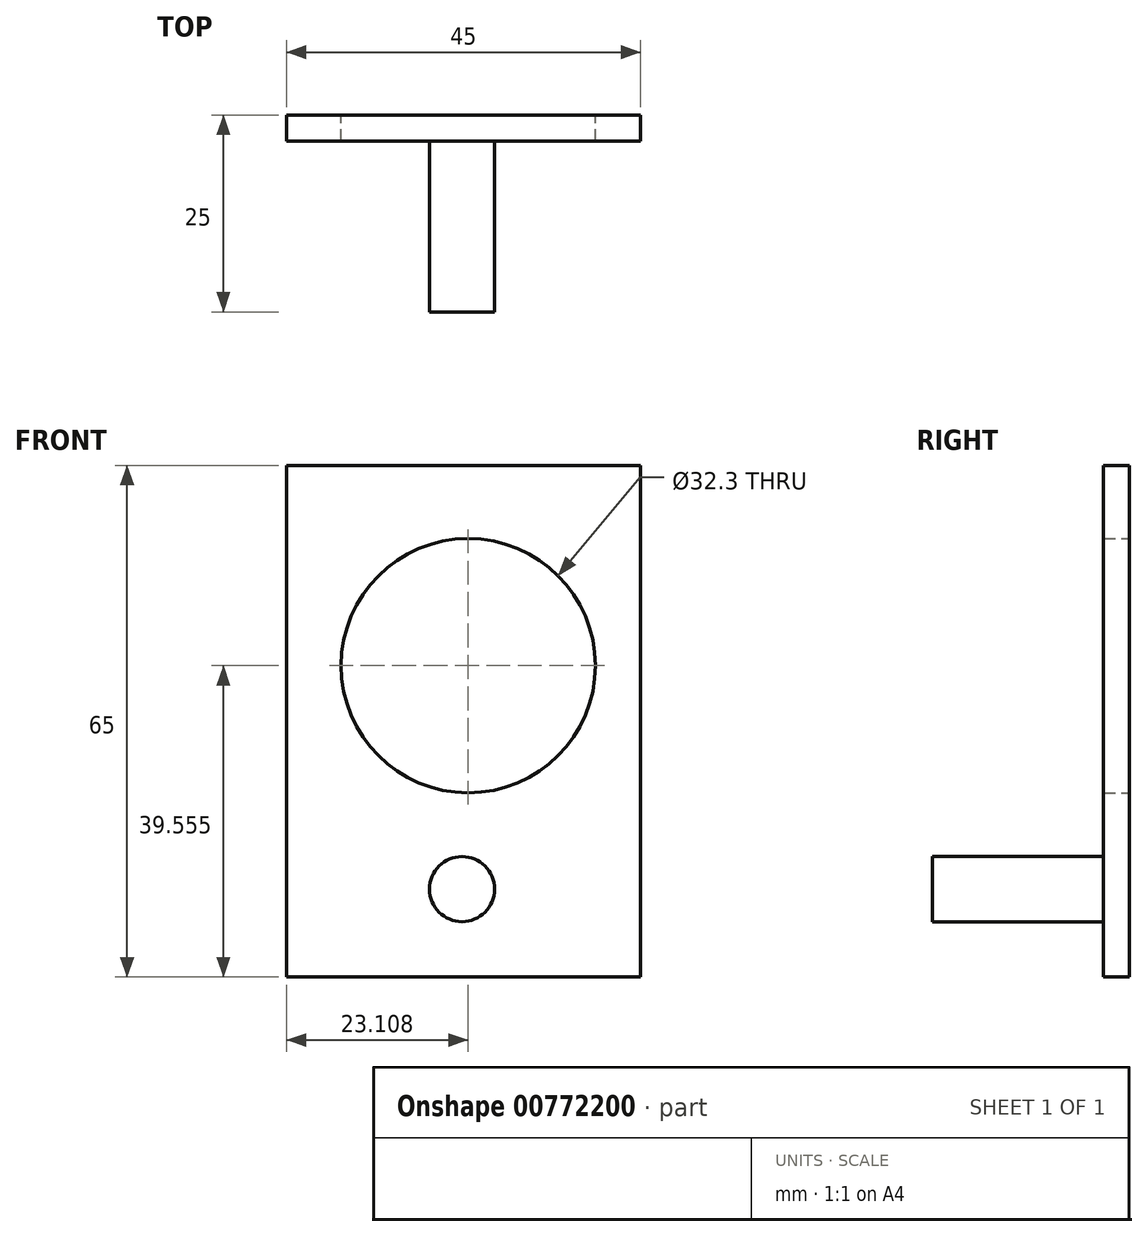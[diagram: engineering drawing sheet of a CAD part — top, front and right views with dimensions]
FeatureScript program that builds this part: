
annotation { "Feature Type Name" : "Feature", "Feature Type Description" : "" }
export const myFeature = defineFeature(function(context is Context, id is Id, definition is map)
    precondition{}
    {
        {
            var Q0;
            Q0=qCreatedBy(makeId("Front.planeOp"),FACE);
            var sketch = newSketch(context, id + "F0", { "sketchPlane" : qUnion([Q0])});
            skLineSegment(sketch, "E0.bottom", {"start": v(-33.82, 36.51) * mm, "end": v(11.18, 36.51) * mm});
            skLineSegment(sketch, "E0.top", {"start": v(-33.82, -28.49) * mm, "end": v(11.18, -28.49) * mm});
            skLineSegment(sketch, "E0.left", {"start": v(-33.82, 36.51) * mm, "end": v(-33.82, -28.49) * mm});
            skLineSegment(sketch, "E0.right", {"start": v(11.18, 36.51) * mm, "end": v(11.18, -28.49) * mm});
            skCircle(sketch, "E1", {"center": v(-10.71, 11.07) * mm, "radius": 16.15 * mm});
            skCircle(sketch, "E2", {"center": v(-11.5, -17.32) * mm, "radius": 4.14 * mm});
            skSolve(sketch);
        }
        {
            var Q0;
            Q0=makeQuery(id+"F0.imprint","IMPRINT",FACE,{"disambiguationData":[TD([[makeQuery(id+"F0.imprint","IMPRINT",EDGE,{"derivedFrom":sQuery(id+"F0.wireOp",EDGE,"E2")}),1.0]])]});
            extrude(context, id + "F1", {"entities" : qUnion([Q0]), "depth" : 25 * mm, "offsetDistance" : 25 * mm});
        }
        {
            var Q0;
            Q0 = qSketchRegion(id + "F0", true);
            extrude(context, id + "F2", {"entities" : qUnion([Q0]), "operationType" : NewBodyOperationType.ADD, "depth" : 3.3 * mm, "offsetDistance" : 25 * mm});
        }
    });
